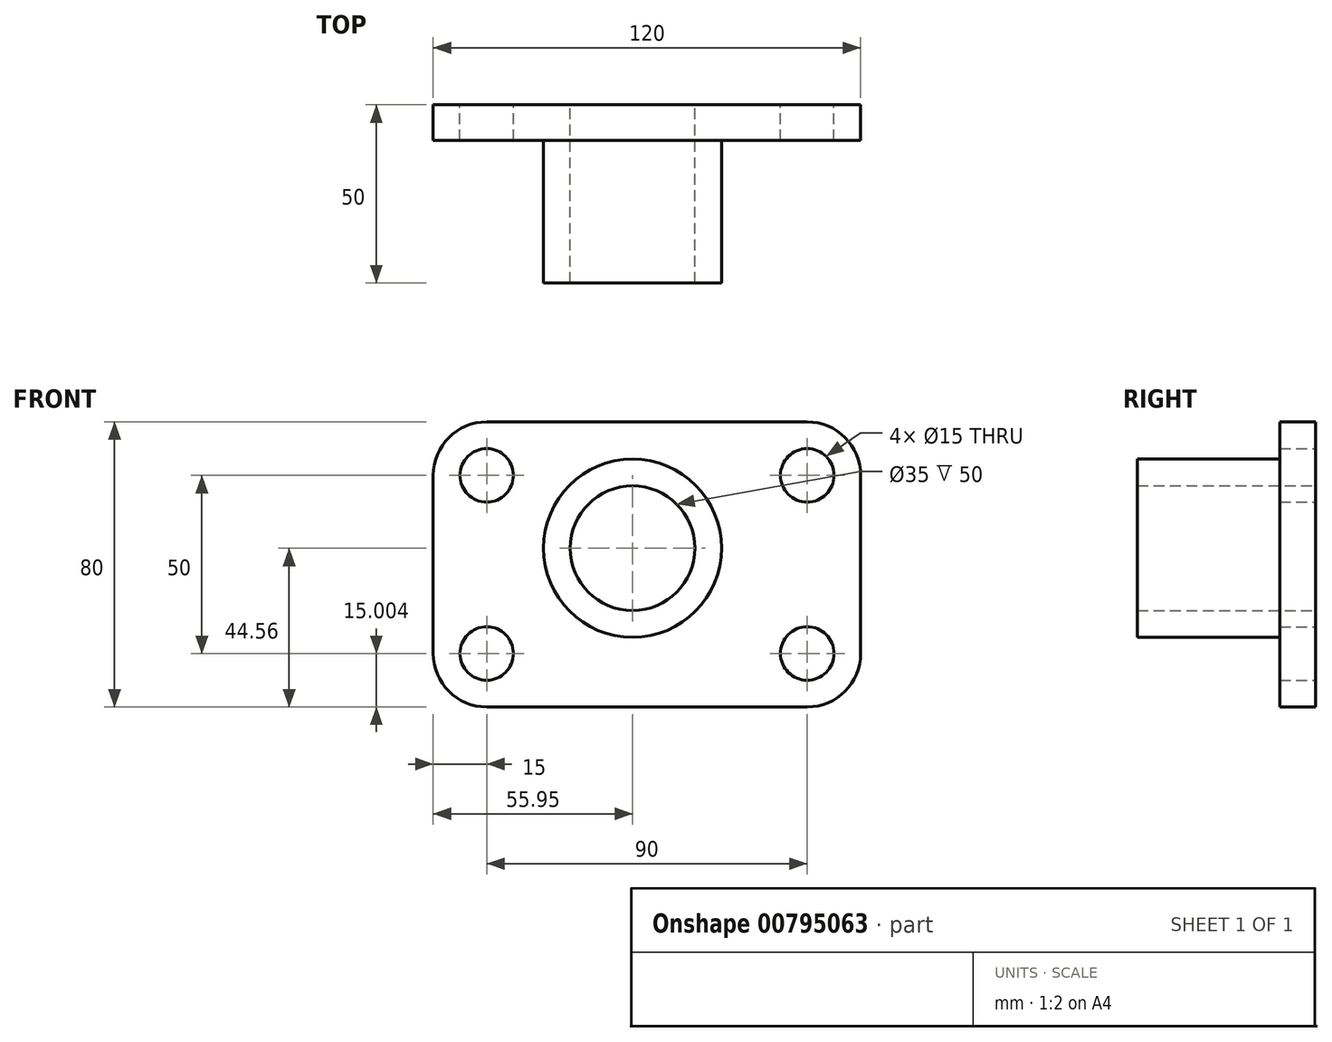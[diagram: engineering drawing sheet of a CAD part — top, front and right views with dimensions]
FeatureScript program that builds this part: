
annotation { "Feature Type Name" : "Feature", "Feature Type Description" : "" }
export const myFeature = defineFeature(function(context is Context, id is Id, definition is map)
    precondition{}
    {
        {
            var Q0;
            Q0=qCreatedBy(makeId("Front.planeOp"),FACE);
            var sketch = newSketch(context, id + "F0", { "sketchPlane" : qUnion([Q0])});
            skLineSegment(sketch, "E0.bottom", {"start": v(-40.95, 35.44) * mm, "end": v(49.05, 35.44) * mm});
            skLineSegment(sketch, "E0.top", {"start": v(-40.95, -44.56) * mm, "end": v(49.05, -44.56) * mm});
            skLineSegment(sketch, "E0.left", {"start": v(-55.95, 20.44) * mm, "end": v(-55.95, -29.56) * mm});
            skLineSegment(sketch, "E0.right", {"start": v(64.05, 20.44) * mm, "end": v(64.05, -29.56) * mm});
            skPoint(sketch, "E1.visualSharp", {"position": v(-55.95, 35.44) * mm});
            skArc(sketch, "E1.filletArc", {"start": v(-40.95, 35.44) * mm, "mid": v(-51.56, 31.05) * mm, "end": v(-55.95, 20.44) * mm});
            skPoint(sketch, "E2.visualSharp", {"position": v(64.05, 35.44) * mm});
            skArc(sketch, "E2.filletArc", {"start": v(64.05, 20.44) * mm, "mid": v(59.66, 31.05) * mm, "end": v(49.05, 35.44) * mm});
            skPoint(sketch, "E3.visualSharp", {"position": v(64.05, -44.56) * mm});
            skArc(sketch, "E3.filletArc", {"start": v(49.05, -44.56) * mm, "mid": v(59.66, -40.16) * mm, "end": v(64.05, -29.56) * mm});
            skPoint(sketch, "E4.visualSharp", {"position": v(-55.95, -44.56) * mm});
            skArc(sketch, "E4.filletArc", {"start": v(-55.95, -29.56) * mm, "mid": v(-51.56, -40.16) * mm, "end": v(-40.95, -44.56) * mm});
            skCircle(sketch, "E5", {"center": v(0, 0) * mm, "radius": 17.5 * mm});
            skCircle(sketch, "E6", {"center": v(0, 0) * mm, "radius": 25 * mm});
            skCircle(sketch, "E7", {"center": v(-40.95, 20.44) * mm, "radius": 7.5 * mm});
            skCircle(sketch, "E8", {"center": v(49.05, 20.44) * mm, "radius": 7.5 * mm});
            skCircle(sketch, "E9", {"center": v(49.05, -29.56) * mm, "radius": 7.5 * mm});
            skCircle(sketch, "E10", {"center": v(-40.95, -29.56) * mm, "radius": 7.5 * mm});
            skSolve(sketch);
        }
        {
            var Q0;
            Q0=makeQuery(id+"F0.imprint","IMPRINT",FACE,{"disambiguationData":[TD([[makeQuery(id+"F0.imprint","IMPRINT",EDGE,{"derivedFrom":sQuery(id+"F0.wireOp",EDGE,"E5")}),-1.0]])]});
            extrude(context, id + "F1", {"entities" : qUnion([Q0]), "depth" : 50 * mm, "offsetDistance" : 25 * mm});
        }
        {
            var Q0;
            Q0=makeQuery(id+"F0.imprint","IMPRINT",FACE,{"disambiguationData":[TD([[makeQuery(id+"F0.imprint","IMPRINT",EDGE,{"derivedFrom":sQuery(id+"F0.wireOp",EDGE,"E5")}),1.0]])]});
            extrude(context, id + "F2", {"entities" : qUnion([Q0]), "operationType" : NewBodyOperationType.REMOVE, "endBound" : BoundingType.THROUGH_ALL, "oppositeDirection" : true, "depth" : 25 * mm, "offsetDistance" : 25 * mm});
        }
        {
            var Q0;
            Q0=makeQuery(id+"F0.imprint","IMPRINT",FACE,{"disambiguationData":[TD([[makeQuery(id+"F0.imprint","IMPRINT",EDGE,{"derivedFrom":sQuery(id+"F0.wireOp",EDGE,"E0.bottom")}),-1.0]])]});
            extrude(context, id + "F3", {"entities" : qUnion([Q0]), "operationType" : NewBodyOperationType.ADD, "depth" : 10 * mm, "offsetDistance" : 25 * mm});
        }
    });
